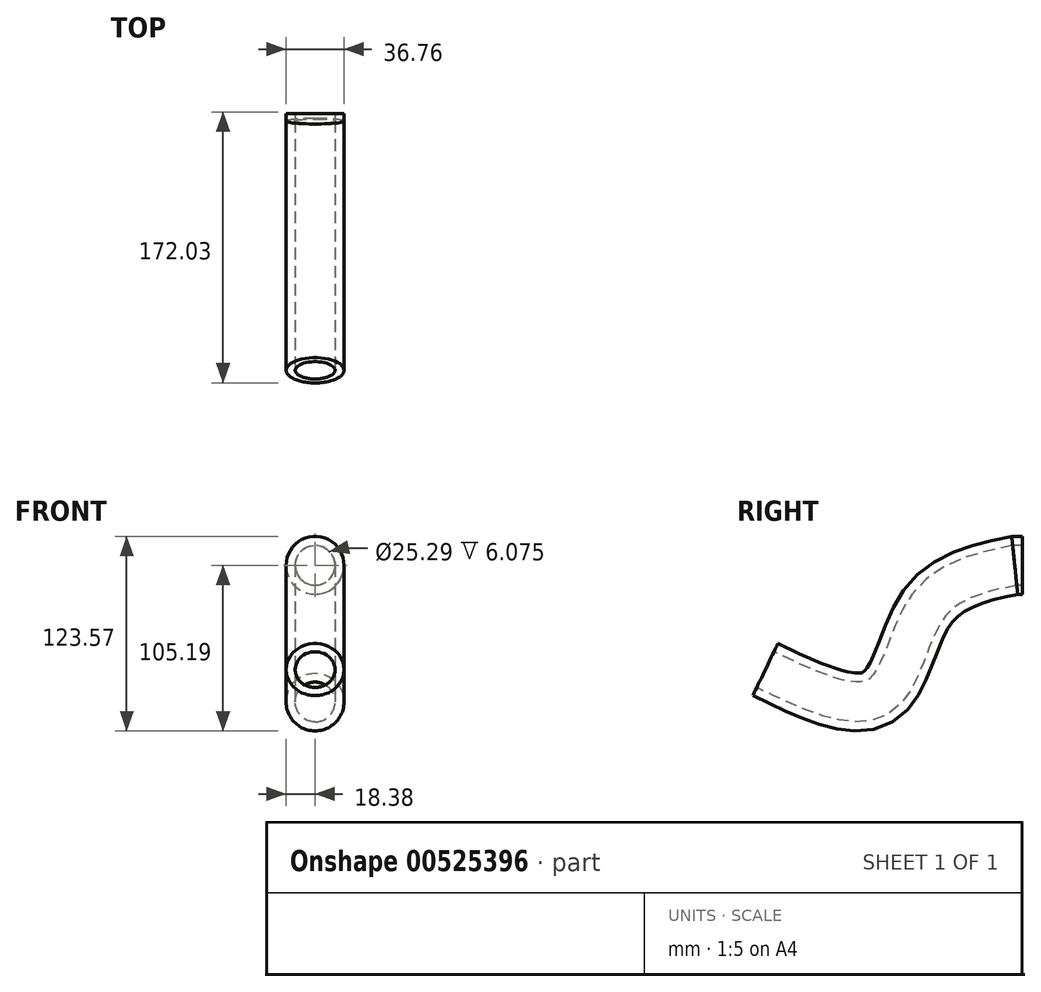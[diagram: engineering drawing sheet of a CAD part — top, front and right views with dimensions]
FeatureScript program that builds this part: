
annotation { "Feature Type Name" : "Feature", "Feature Type Description" : "" }
export const myFeature = defineFeature(function(context is Context, id is Id, definition is map)
    precondition{}
    {
        {
            var Q0;
            Q0=qCreatedBy(makeId("Front.planeOp"),FACE);
            var sketch = newSketch(context, id + "F0", { "sketchPlane" : qUnion([Q0])});
            skCircle(sketch, "E0", {"center": v(0, 49.29) * mm, "radius": 18.38 * mm});
            skCircle(sketch, "E1", {"center": v(0, 49.29) * mm, "radius": 12.65 * mm});
            skSolve(sketch);
        }
        {
            var Q0;
            Q0=qCreatedBy(makeId("Right.planeOp"),FACE);
            var sketch = newSketch(context, id + "F1", { "sketchPlane" : qUnion([Q0])});
            skLineSegment(sketch, "E2", {"start": v(0, 49.86) * mm, "end": v(-4.82, 49.86) * mm});
            skFitSpline(sketch, "E3", {"points": [v(-4.82, 49.86) * mm, v(-60.05, 24.08) * mm, v(-91.21, -33.43) * mm, v(-162.88, -16.43) * mm], "startDerivative": vector(-200.8, -42.28) * mm, "endDerivative": vector(-240.1, 116.03) * mm});
            skSolve(sketch);
        }
        {
            var Q0;
            Q0 = qSketchRegion(id + "F0", true);
            var Q1;
            Q1 = qConstructionFilter(qBodyType(qCreatedBy(id + "F1" ,EDGE), BodyType.WIRE), ConstructionObject.NO);
            sweep(context, id + "F2", {"profiles" : qUnion([Q0]), "path" : qUnion([Q1])});
        }
    });
